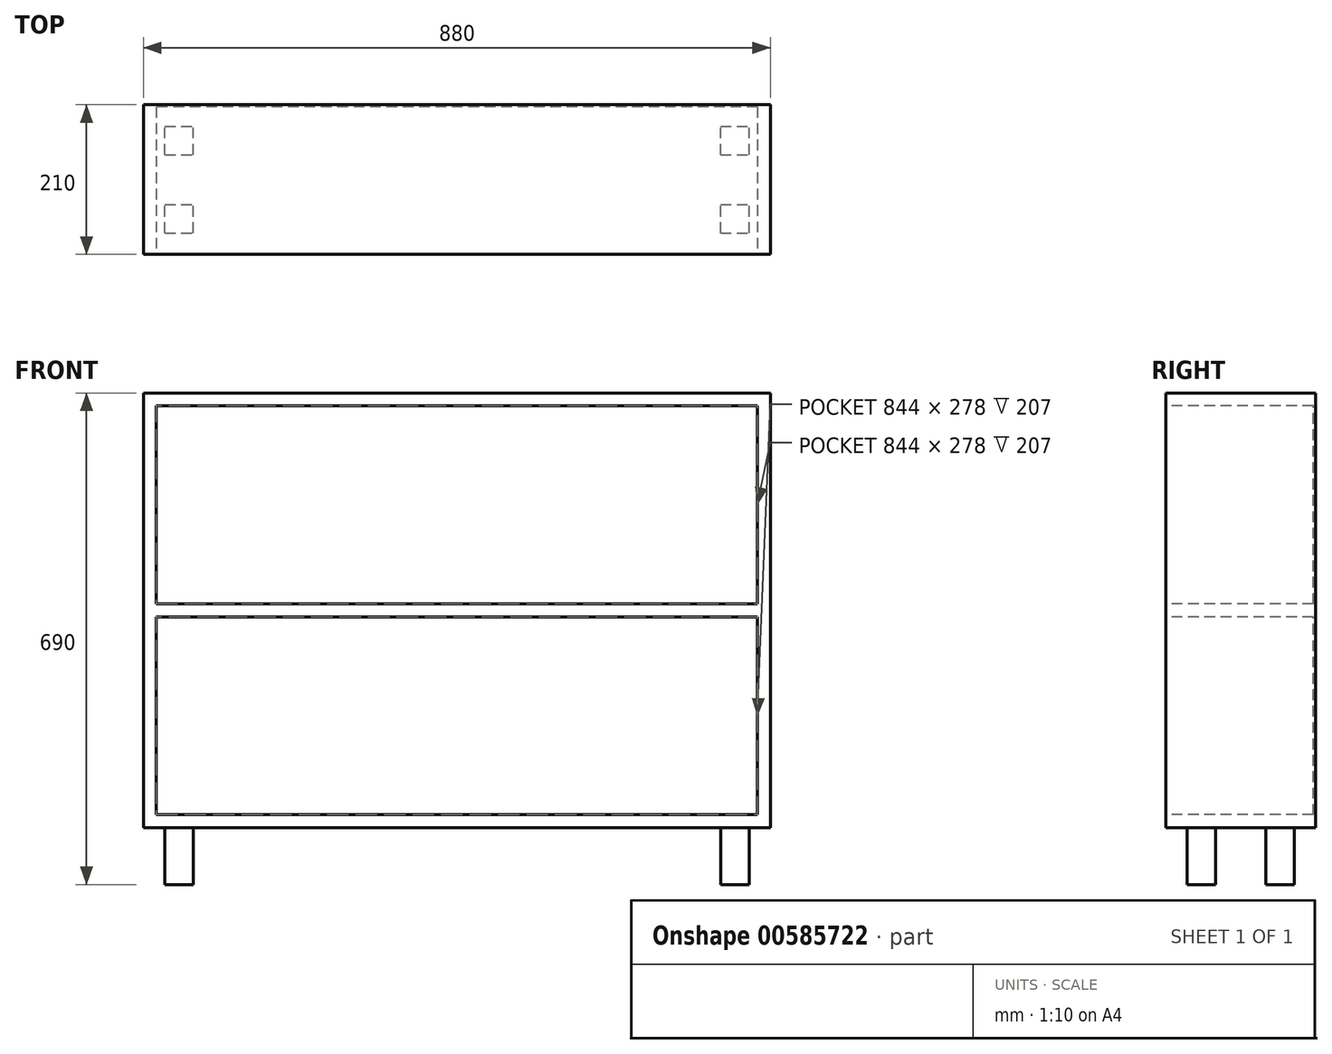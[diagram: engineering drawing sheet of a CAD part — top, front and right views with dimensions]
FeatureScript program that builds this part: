
annotation { "Feature Type Name" : "Feature", "Feature Type Description" : "" }
export const myFeature = defineFeature(function(context is Context, id is Id, definition is map)
    precondition{}
    {
        {
            var Q0;
            Q0=qCreatedBy(makeId("Front.planeOp"),FACE);
            var sketch = newSketch(context, id + "F0", { "sketchPlane" : qUnion([Q0])});
            skLineSegment(sketch, "E0.bottom", {"start": v(-37.9, 657.21) * mm, "end": v(842.1, 657.21) * mm});
            skLineSegment(sketch, "E0.top", {"start": v(-37.9, -32.79) * mm, "end": v(842.1, -32.79) * mm});
            skLineSegment(sketch, "E0.left", {"start": v(-37.9, 657.21) * mm, "end": v(-37.9, -32.79) * mm});
            skLineSegment(sketch, "E0.right", {"start": v(842.1, 657.21) * mm, "end": v(842.1, -32.79) * mm});
            skSolve(sketch);
        }
        {
            var Q0;
            Q0=makeQuery(id+"F0.imprint","IMPRINT",FACE,{"disambiguationData":[TD([[makeQuery(id+"F0.imprint","IMPRINT",EDGE,{"derivedFrom":sQuery(id+"F0.wireOp",EDGE,"E0.bottom")}),-1.0]])]});
            extrude(context, id + "F1", {"entities" : qUnion([Q0]), "depth" : 210 * mm, "offsetDistance" : 25 * mm});
        }
        {
            var Q0;
            Q0=makeQuery(id+"F1.opExtrude","SWEPT_FACE",FACE,{"disambiguationData":[OSD([sQuery(id+"F0.wireOp",EDGE,"E0.top")])]});
            var sketch = newSketch(context, id + "F2", { "sketchPlane" : qUnion([Q0])});
            skLineSegment(sketch, "E1.bottom", {"start": v(-37.9, 210) * mm, "end": v(842.1, 210) * mm});
            skLineSegment(sketch, "E1.top", {"start": v(-37.9, 0) * mm, "end": v(842.1, 0) * mm});
            skLineSegment(sketch, "E1.left", {"start": v(-37.9, 210) * mm, "end": v(-37.9, 0) * mm});
            skLineSegment(sketch, "E1.right", {"start": v(842.1, 210) * mm, "end": v(842.1, 0) * mm});
            skLineSegment(sketch, "E2.bottom", {"start": v(-7.9, 180) * mm, "end": v(32.1, 180) * mm});
            skLineSegment(sketch, "E2.top", {"start": v(-7.9, 140) * mm, "end": v(32.1, 140) * mm});
            skLineSegment(sketch, "E2.left", {"start": v(-7.9, 180) * mm, "end": v(-7.9, 140) * mm});
            skLineSegment(sketch, "E2.right", {"start": v(32.1, 180) * mm, "end": v(32.1, 140) * mm});
            skLineSegment(sketch, "E3.0.1.0", {"start": v(32.1, 70) * mm, "end": v(32.1, 30) * mm});
            skLineSegment(sketch, "E3.0.1.1", {"start": v(-7.9, 70) * mm, "end": v(-7.9, 30) * mm});
            skLineSegment(sketch, "E3.0.1.2", {"start": v(-7.9, 30) * mm, "end": v(32.1, 30) * mm});
            skLineSegment(sketch, "E3.0.1.3", {"start": v(-7.9, 70) * mm, "end": v(32.1, 70) * mm});
            skLineSegment(sketch, "E3.1.0.0", {"start": v(812.1, 180) * mm, "end": v(812.1, 140) * mm});
            skLineSegment(sketch, "E3.1.0.1", {"start": v(772.1, 180) * mm, "end": v(772.1, 140) * mm});
            skLineSegment(sketch, "E3.1.0.2", {"start": v(772.1, 140) * mm, "end": v(812.1, 140) * mm});
            skLineSegment(sketch, "E3.1.0.3", {"start": v(772.1, 180) * mm, "end": v(812.1, 180) * mm});
            skLineSegment(sketch, "E3.1.1.0", {"start": v(812.1, 70) * mm, "end": v(812.1, 30) * mm});
            skLineSegment(sketch, "E3.1.1.1", {"start": v(772.1, 70) * mm, "end": v(772.1, 30) * mm});
            skLineSegment(sketch, "E3.1.1.2", {"start": v(772.1, 30) * mm, "end": v(812.1, 30) * mm});
            skLineSegment(sketch, "E3.1.1.3", {"start": v(772.1, 70) * mm, "end": v(812.1, 70) * mm});
            skLineSegment(sketch, "E3.direction1", {"start": v(-7.9, 140) * mm, "end": v(772.1, 140) * mm, "construction": true});
            skLineSegment(sketch, "E3.direction2", {"start": v(-7.9, 140) * mm, "end": v(-7.9, 30) * mm, "construction": true});
            skSolve(sketch);
        }
        {
            var Q0;
            Q0=makeQuery(id+"F2.imprint","IMPRINT",FACE,{"disambiguationData":[TD([[makeQuery(id+"F2.imprint","IMPRINT",EDGE,{"derivedFrom":sQuery(id+"F2.wireOp",EDGE,"E1.bottom")}),-1.0]])]});
            extrude(context, id + "F3", {"entities" : qUnion([Q0]), "operationType" : NewBodyOperationType.REMOVE, "oppositeDirection" : true, "depth" : 80 * mm, "offsetDistance" : 25 * mm});
        }
        {
            var Q0;
            Q0=makeQuery(id+"F1.opExtrude","CAP_FACE",FACE,{"disambiguationData":[OSD([sQuery(id+"F0.wireOp",EDGE,"E0.bottom"),sQuery(id+"F0.wireOp",EDGE,"E0.top"),sQuery(id+"F0.wireOp",EDGE,"E0.left"),sQuery(id+"F0.wireOp",EDGE,"E0.right")])],"isStart":false});
            var sketch = newSketch(context, id + "F4", { "sketchPlane" : qUnion([Q0])});
            skLineSegment(sketch, "E4.bottom", {"start": v(-19.9, 639.21) * mm, "end": v(824.1, 639.21) * mm});
            skLineSegment(sketch, "E4.top", {"start": v(-19.9, 361.21) * mm, "end": v(824.1, 361.21) * mm});
            skLineSegment(sketch, "E4.left", {"start": v(-19.9, 639.21) * mm, "end": v(-19.9, 361.21) * mm});
            skLineSegment(sketch, "E4.right", {"start": v(824.1, 639.21) * mm, "end": v(824.1, 361.21) * mm});
            skLineSegment(sketch, "E5.0.1.0", {"start": v(824.1, 343.21) * mm, "end": v(824.1, 65.21) * mm});
            skLineSegment(sketch, "E5.0.1.1", {"start": v(-19.9, 343.21) * mm, "end": v(-19.9, 65.21) * mm});
            skLineSegment(sketch, "E5.0.1.2", {"start": v(-19.9, 65.21) * mm, "end": v(824.1, 65.21) * mm});
            skLineSegment(sketch, "E5.0.1.3", {"start": v(-19.9, 343.21) * mm, "end": v(824.1, 343.21) * mm});
            skLineSegment(sketch, "E5.direction1", {"start": v(-19.9, 361.21) * mm, "end": v(86.1, 361.21) * mm, "construction": true});
            skLineSegment(sketch, "E5.direction2", {"start": v(-19.9, 361.21) * mm, "end": v(-19.9, 65.21) * mm, "construction": true});
            skLineSegment(sketch, "E6", {"start": v(-37.9, 47.21) * mm, "end": v(842.1, 47.21) * mm, "construction": true});
            skSolve(sketch);
        }
        {
            var Q0;
            Q0=makeQuery(id+"F4.imprint","IMPRINT",FACE,{"disambiguationData":[TD([[makeQuery(id+"F4.imprint","IMPRINT",EDGE,{"derivedFrom":sQuery(id+"F4.wireOp",EDGE,"E4.bottom")}),-1.0]])]});
            var Q1;
            Q1=makeQuery(id+"F4.imprint","IMPRINT",FACE,{"disambiguationData":[TD([[makeQuery(id+"F4.imprint","IMPRINT",EDGE,{"derivedFrom":sQuery(id+"F4.wireOp",EDGE,"E5.0.1.0")}),-1.0]])]});
            var Q2;
            Q2=makeQuery(id+"F4.imprint","IMPRINT",FACE,{"disambiguationData":[TD([[makeQuery(id+"F4.imprint","IMPRINT",EDGE,{"derivedFrom":sQuery(id+"F4.wireOp",EDGE,"E5.0.2.0")}),-1.0]])]});
            var Q3;
            Q3=makeQuery(id+"F1.opExtrude","CAP_FACE",FACE,{"disambiguationData":[OSD([sQuery(id+"F0.wireOp",EDGE,"E0.bottom"),sQuery(id+"F0.wireOp",EDGE,"E0.top"),sQuery(id+"F0.wireOp",EDGE,"E0.left"),sQuery(id+"F0.wireOp",EDGE,"E0.right")])],"isStart":true});
            extrude(context, id + "F5", {"entities" : qUnion([Q0, Q1, Q2]), "operationType" : NewBodyOperationType.REMOVE, "endBound" : BoundingType.UP_TO_SURFACE, "oppositeDirection" : true, "depth" : 25 * mm, "endBoundEntityFace" : qUnion([Q3]), "hasOffset" : true, "offsetDistance" : 3 * mm});
        }
    });
